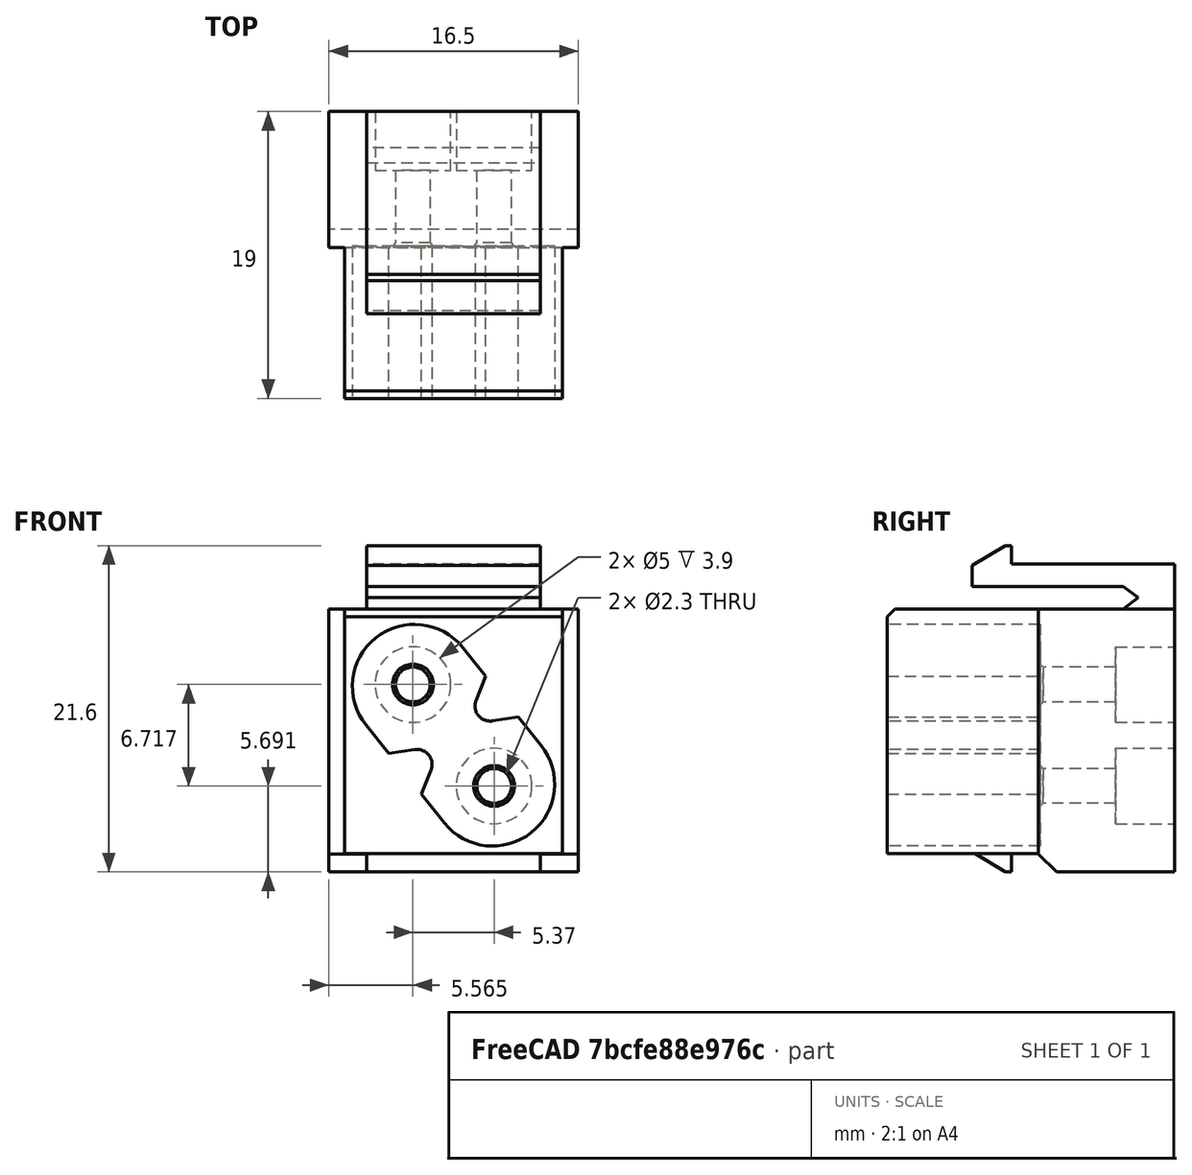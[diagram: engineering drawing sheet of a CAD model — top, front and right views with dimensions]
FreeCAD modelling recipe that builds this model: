
FCSTD DOCUMENT  (FreeCAD 1.0R39319 (Git))
Label: IEC_C8_Keystone
License: All rights reserved
LicenseURL: https://en.wikipedia.org/wiki/All_rights_reserved
objects: Sketcher::SketchObject×4, PartDesign::Pad×3, PartDesign::Pocket×3, PartDesign::Chamfer×2, Part::Feature×1, PartDesign::FeatureBase×1, PartDesign::Body×1, App::Part×1, App::FeaturePython×1, Assembly::JointGroup×1, Assembly::AssemblyObject×1
note: 36 computed .brp shape members not serialized (recipe doc carries the construction recipe); baked Part::Feature solids carry a one-line shape summary decoded from their .brp

FEATURE [Part::Feature] keystone_blank_insert_chamfer002_solid  label="keystone_blank_insert_chamfer002 (Solid)"
  shape: bbox 16.5 x 19 x 21.6 mm, 39 faces (baked)
FEATURE [PartDesign::FeatureBase] BaseFeature
  BaseFeature = -> keystone_blank_insert_chamfer002_solid
  Suppressed = false
FEATURE [PartDesign::Pad] Pad
  BaseFeature = -> BaseFeature
  Direction = (0,-1,0)
  Length = 10
  Length2 = 10
  Profile = -> BaseFeature [Face3]
  Refine = true
  Reversed = true
  Suppressed = false
  Type = 3
  UpToFace = -> BaseFeature [Face26]
FEATURE [PartDesign::Pad] Pad001
  BaseFeature = -> Pad
  Direction = (0,0,-1)
  Length = 10
  Length2 = 10
  Profile = -> Pad [Face14,Face11]
  Refine = true
  Suppressed = false
  Type = 3
  UpToFace = -> Pad [Face3]
FEATURE [Sketcher::SketchObject] Sketch
  ArcFitTolerance = 1e-06
  AttachmentSupport = -> [Pad001]
  ExternalGeometry = -> [Pad001]
  FullyConstrained = true
  MakeInternals = false
  MapMode = 5
  Placement = pos=(0,19,0) rot=(0,0.707107,0.707107;3.14159rad)
  sketch-geometry (4):
    g0: LineSegment StartX=-15.45 StartY=1.42e-14 StartZ=0 EndX=-15.45 EndY=-1.2 EndZ=0
    g1: LineSegment StartX=-15.45 StartY=-1.2 StartZ=0 EndX=1.05 EndY=-1.2 EndZ=0
    g2: LineSegment StartX=1.05 StartY=-1.2 StartZ=0 EndX=1.05 EndY=1.42e-14 EndZ=0
    g3: LineSegment StartX=1.05 StartY=1.42e-14 StartZ=0 EndX=-15.45 EndY=1.42e-14 EndZ=0
  constraints (11):
    c: Coincident(g0,g1)
    c: Coincident(g1,g2)
    c: Coincident(g2,g3)
    c: Coincident(g3,g0)
    c: Vertical(g0)
    c: Vertical(g2)
    c: Horizontal(g1)
    c: Horizontal(g3)
    c: Coincident(g0,g-3)
    c: PointOnObject(g-3,g2)
    c: DistanceY(g0,g0) = 1.2
FEATURE [PartDesign::Pad] Pad002
  BaseFeature = -> Pad001
  Direction = (0,1,-2e-16)
  Length = 10
  Length2 = 10
  Profile = -> Sketch
  ReferenceAxis = -> Sketch [N_Axis]
  Refine = true
  Reversed = true
  Suppressed = false
  Type = 3
  UpToFace = -> Pad001 [Face26]
FEATURE [Sketcher::SketchObject] Sketch001
  ArcFitTolerance = 1e-06
  AttachmentSupport = -> [Pad002]
  ExternalGeometry = -> [Pad002]
  FullyConstrained = true
  MakeInternals = false
  MapMode = 5
  Placement = pos=(0,0,0) rot=(1,0,0;1.5708rad)
  sketch-geometry (32):
    g0: LineSegment [constr] StartX=9.88511 StartY=4.4914 StartZ=0 EndX=4.51489 EndY=11.2086 EndZ=0
    g1: LineSegment [constr] StartX=15.554 StartY=3.96639 StartZ=0 EndX=5.25073 EndY=16.854 EndZ=0
    g2: LineSegment [constr] StartX=5.25073 StartY=16.854 StartZ=0 EndX=-1.15405 EndY=11.7336 EndZ=0
    g3: LineSegment [constr] StartX=-1.15405 StartY=11.7336 StartZ=0 EndX=9.14927 EndY=-1.15405 EndZ=0
    g4: LineSegment [constr] StartX=9.14927 StartY=-1.15405 StartZ=0 EndX=15.554 EndY=3.96639 EndZ=0
    g5: GeomPoint [constr] X=7.2 Y=7.85 Z=0
    g6: LineSegment [constr] StartX=3.99761 StartY=5.28978 StartZ=0 EndX=5.55975 EndY=6.53867 EndZ=0
    g7: LineSegment [constr] StartX=10.4024 StartY=10.4102 StartZ=0 EndX=8.84025 EndY=9.16133 EndZ=0
    g8: ArcOfCircle CenterX=9.79144 CenterY=4.60856 CenterZ=0 NormalX=0 NormalY=0 NormalZ=1 AngleXU=0 Radius=4.1 StartAngle=3.81601 EndAngle=6.9576
    g9: ArcOfCircle CenterX=4.77868 CenterY=5.91423 CenterZ=0 NormalX=0 NormalY=0 NormalZ=1 AngleXU=0 Radius=1 StartAngle=5.91041 EndAngle=6.9576
    g10: LineSegment StartX=5.71 StartY=5.55002 StartZ=0 EndX=5.07918 EndY=3.93693 EndZ=0
    g11: LineSegment StartX=6.58905 StartY=2.04834 StartZ=0 EndX=5.07918 EndY=3.93693 EndZ=0
    g12: ArcOfCircle CenterX=4.77868 CenterY=5.91423 CenterZ=0 NormalX=0 NormalY=0 NormalZ=1 AngleXU=0 Radius=1 StartAngle=0.674419 EndAngle=1.72162
    g13: LineSegment StartX=4.62843 StartY=6.90287 StartZ=0 EndX=2.91604 EndY=6.64263 EndZ=0
    g14: LineSegment [constr] StartX=5.71 StartY=5.55002 StartZ=0 EndX=4.62843 EndY=6.90287 EndZ=0
    g15: LineSegment StartX=12.9938 StartY=7.16878 StartZ=0 EndX=11.484 EndY=9.05737 EndZ=0
    g16: LineSegment StartX=9.77157 StartY=8.79713 StartZ=0 EndX=11.484 EndY=9.05737 EndZ=0
    g17: ArcOfCircle CenterX=9.62132 CenterY=9.78577 CenterZ=0 NormalX=0 NormalY=0 NormalZ=1 AngleXU=0 Radius=1 StartAngle=3.81601 EndAngle=4.86321
    g18: ArcOfCircle CenterX=9.62132 CenterY=9.78577 CenterZ=0 NormalX=0 NormalY=0 NormalZ=1 AngleXU=0 Radius=1 StartAngle=2.76881 EndAngle=3.81601
    g19: LineSegment StartX=8.69 StartY=10.15 StartZ=0 EndX=9.32082 EndY=11.7631 EndZ=0
    g20: LineSegment [constr] StartX=9.77157 StartY=8.79713 StartZ=0 EndX=8.69 EndY=10.15 EndZ=0
    g21: LineSegment StartX=1.40617 StartY=8.53122 StartZ=0 EndX=2.91604 EndY=6.64263 EndZ=0
    g22: ArcOfCircle CenterX=4.60856 CenterY=11.0914 CenterZ=0 NormalX=0 NormalY=0 NormalZ=1 AngleXU=0 Radius=4.1 StartAngle=0.674419 EndAngle=3.81601
    g23: LineSegment StartX=7.81095 StartY=13.6517 StartZ=0 EndX=9.32082 EndY=11.7631 EndZ=0
    g24: LineSegment [constr] StartX=0 StartY=16.2 StartZ=0 EndX=0 EndY=0 EndZ=0
    g25: LineSegment [constr] StartX=0 StartY=0 StartZ=0 EndX=14.4 EndY=0 EndZ=0
    g26: LineSegment [constr] StartX=14.4 StartY=0 StartZ=0 EndX=14.4 EndY=16.2 EndZ=0
    g27: LineSegment [constr] StartX=14.4 StartY=16.2 StartZ=0 EndX=0 EndY=16.2 EndZ=0
    g28: LineSegment [constr] StartX=4.60856 StartY=15.1914 StartZ=0 EndX=4.60856 EndY=15.7 EndZ=0
    g29: LineSegment [constr] StartX=9.79144 StartY=0.508559 StartZ=0 EndX=9.79144 EndY=0 EndZ=0
    g30: LineSegment [constr] StartX=13.8914 StartY=4.60856 StartZ=0 EndX=14.4 EndY=4.60856 EndZ=0
    g31: LineSegment [constr] StartX=0.508559 StartY=11.0914 StartZ=0 EndX=0 EndY=11.0914 EndZ=0
  constraints (88):
    c: Coincident(g1,g2)
    c: Coincident(g2,g3)
    c: Coincident(g3,g4)
    c: Coincident(g4,g1)
    c: Symmetric(g3,g1,g5)
    c: Distance(g2,g4) = 16.5
    c: Distance(g1,g3) = 8.2
    c: Symmetric(g0,g0,g5)
    c: Symmetric(g3,g3,g6)
    c: Symmetric(g1,g1,g7)
    c: Equal(g7,g6)
    c: PointOnObject(g8,g0)
    c: Tangent(g8,g4)
    c: Tangent(g8,g3) = -1.5708
    c: Tangent(g8,g1) = -1.5708
    c: PointOnObject(g9,g6)
    c: Coincident(g9,g6)
    c: Coincident(g10,g9)
    c: Tangent(g11,g8) = 1.5708
    c: Coincident(g10,g11)
    c: Radius(g9) = 1
    c: Coincident(g12,g9)
    c: Coincident(g12,g6)
    c: PointOnObject(g13,g3)
    c: Tangent(g13,g12) = -1.5708
    c: Equal(g10,g13)
    c: Angle(g13,g10) = 1.0472
    c: Coincident(g14,g9)
    c: Coincident(g14,g12)
    c: Perpendicular(g14,g6)
    c: Coincident(g16,g15)
    c: Radius(g17) = 1
    c: Coincident(g18,g17)
    c: Tangent(g19,g18) = 1.5708
    c: Equal(g16,g19)
    c: Angle(g19,g16) = -1.0472
    c: Coincident(g15,g8)
    c: PointOnObject(g15,g1)
    c: Coincident(g18,g17)
    c: Coincident(g18,g7)
    c: Tangent(g16,g17) = -1.5708
    c: PointOnObject(g19,g1)
    c: Coincident(g20,g16)
    c: Coincident(g20,g18)
    c: Equal(g15,g11)
    c: Perpendicular(g3,g4)
    c: Perpendicular(g1,g4)
    c: Perpendicular(g2,g3)
    c: Perpendicular(g3,g6)
    c: Perpendicular(g1,g7)
    c: Symmetric(g8,g22,g6)
    c: Symmetric(g8,g22,g6)
    c: Symmetric(g11,g21,g6)
    c: Symmetric(g11,g21,g6)
    c: Symmetric(g15,g23,g6)
    c: Symmetric(g15,g23,g6)
    c: Tangent(g22,g2)
    c: Distance(g6,g7) = 4.2
    c: Distance(g0,g0) = 8.6
    c: Coincident(g24,g25)
    c: Coincident(g25,g26)
    c: Coincident(g26,g27)
    c: Coincident(g27,g24)
    c: Vertical(g24)
    c: Vertical(g26)
    c: Horizontal(g25)
    c: Horizontal(g27)
    c: Coincident(g24,g-3)
    c: Coincident(g25,g-4)
    c: PointOnObject(g28,g22)
    c: PointOnObject(g28,g-5)
    c: Vertical(g28)
    c: PointOnObject(g29,g8)
    c: PointOnObject(g29,g25)
    c: Perpendicular(g25,g29)
    c: Equal(g28,g29)
    c: PointOnObject(g30,g8)
    c: PointOnObject(g30,g26)
    c: Horizontal(g30)
    c: PointOnObject(g31,g22)
    c: PointOnObject(g31,g24)
    c: Horizontal(g31)
    c: Equal(g31,g30)
    c: Perpendicular(g22,g31)
    c: Perpendicular(g22,g28)
    c: Perpendicular(g8,g29)
    c: Perpendicular(g8,g30)
    c: Equal(g28,g31)
FEATURE [PartDesign::Pocket] Pocket
  BaseFeature = -> Pad002
  Direction = (0,1,-2e-16)
  Length = 10.1
  Length2 = 5
  Profile = -> Sketch001
  ReferenceAxis = -> Sketch001 [N_Axis]
  Refine = true
  Suppressed = false
  Type = 0
FEATURE [Sketcher::SketchObject] Sketch002
  ArcFitTolerance = 1e-06
  AttachmentSupport = -> [Pocket]
  FullyConstrained = true
  MakeInternals = false
  MapMode = 5
  Placement = pos=(0,10.1,0) rot=(1,0,0;1.5708rad)
  sketch-geometry (6):
    g0: LineSegment [constr] StartX=4.51489 StartY=11.2086 StartZ=0 EndX=9.88511 EndY=4.4914 EndZ=0
    g1: LineSegment [constr] StartX=4.60856 StartY=11.0914 StartZ=0 EndX=9.79144 EndY=4.60856 EndZ=0
    g2: GeomPoint [constr] X=7.2 Y=7.85 Z=0
    g3: GeomPoint [constr] X=7.2 Y=7.85 Z=0
    g4: Circle CenterX=4.51489 CenterY=11.2086 CenterZ=0 NormalX=0 NormalY=0 NormalZ=1 AngleXU=0 Radius=1.15
    g5: Circle CenterX=9.88511 CenterY=4.4914 CenterZ=0 NormalX=0 NormalY=0 NormalZ=1 AngleXU=0 Radius=1.15
  constraints (11):
    c: Distance(g0,g0) = 8.6
    c: Coincident(g1,g-3)
    c: Coincident(g1,g-4)
    c: Symmetric(g1,g1,g2)
    c: Symmetric(g0,g0,g3)
    c: Coincident(g3,g2)
    c: Parallel(g0,g1)
    c: Diameter(g4) = 2.3
    c: Coincident(g4,g0)
    c: Coincident(g5,g0)
    c: Equal(g5,g4)
FEATURE [PartDesign::Pocket] Pocket001
  BaseFeature = -> Pocket
  Direction = (0,1,-2e-16)
  Length = 5
  Length2 = 5
  Profile = -> Sketch002
  ReferenceAxis = -> Sketch002 [N_Axis]
  Refine = true
  Suppressed = false
  Type = 1
FEATURE [Sketcher::SketchObject] Sketch003
  ArcFitTolerance = 1e-06
  AttachmentSupport = -> [Pocket001]
  ExternalGeometry = -> [Pocket001]
  FullyConstrained = true
  MakeInternals = false
  MapMode = 5
  Placement = pos=(0,19,0) rot=(0,0.707107,0.707107;3.14159rad)
  sketch-geometry (2):
    g0: Circle CenterX=-9.88511 CenterY=4.4914 CenterZ=0 NormalX=0 NormalY=0 NormalZ=1 AngleXU=0 Radius=2.5
    g1: Circle CenterX=-4.51489 CenterY=11.2086 CenterZ=0 NormalX=0 NormalY=0 NormalZ=1 AngleXU=0 Radius=2.5
  constraints (4):
    c: Diameter(g0) = 5
    c: Coincident(g0,g-4)
    c: Coincident(g1,g-3)
    c: Equal(g1,g0)
FEATURE [PartDesign::Pocket] Pocket002
  BaseFeature = -> Pocket001
  Direction = (0,-1,2e-16)
  Length = 0
  Length2 = 5
  Offset = -5
  Profile = -> Sketch003
  ReferenceAxis = -> Sketch003 [N_Axis]
  Refine = true
  Suppressed = false
  Type = 3
  UpToFace = -> Pocket001 [Face36]
FEATURE [PartDesign::Chamfer] Chamfer001
  Angle = 45
  Base = -> Pocket002 [Edge114,Edge115]
  BaseFeature = -> Pocket002
  ChamferType = 0
  FlipDirection = false
  Refine = true
  Size = 0.2
  Size2 = 1
  SupportTransform = false
  Suppressed = false
  UseAllEdges = false
FEATURE [PartDesign::Chamfer] Chamfer002
  Angle = 45
  Base = -> Chamfer001 [Edge77]
  BaseFeature = -> Chamfer001
  ChamferType = 0
  FlipDirection = false
  Refine = true
  Size = 1.19
  Size2 = 1
  SupportTransform = false
  Suppressed = false
  UseAllEdges = false
FEATURE [PartDesign::Body] Body
  AllowCompound = false
  BaseFeature = -> keystone_blank_insert_chamfer002_solid
  Group = -> [BaseFeature,Pad,Pad001,Sketch,Pad002,Sketch001,Pocket,Sketch002,Pocket001,Sketch003,Pocket002,Chamfer001,Chamfer002]
  Origin = -> Origin
  Tip = -> Chamfer002
FEATURE [App::Part] Part  label="Keystone"
  Group = -> [keystone_blank_insert_chamfer002_solid,Body]
  Origin = -> Origin001
FEATURE [App::FeaturePython] GroundedJoint  # Assembly grounded joint (typed FeaturePython)
  ObjectToGround = -> Part
FEATURE [Assembly::JointGroup] Joints
  Group = -> [GroundedJoint]
FEATURE [Assembly::AssemblyObject] Assembly  label="IEC C8 Keystone"
  Group = -> [Joints,Part,GroundedJoint]
  Origin = -> Origin004
  Type = Assembly
